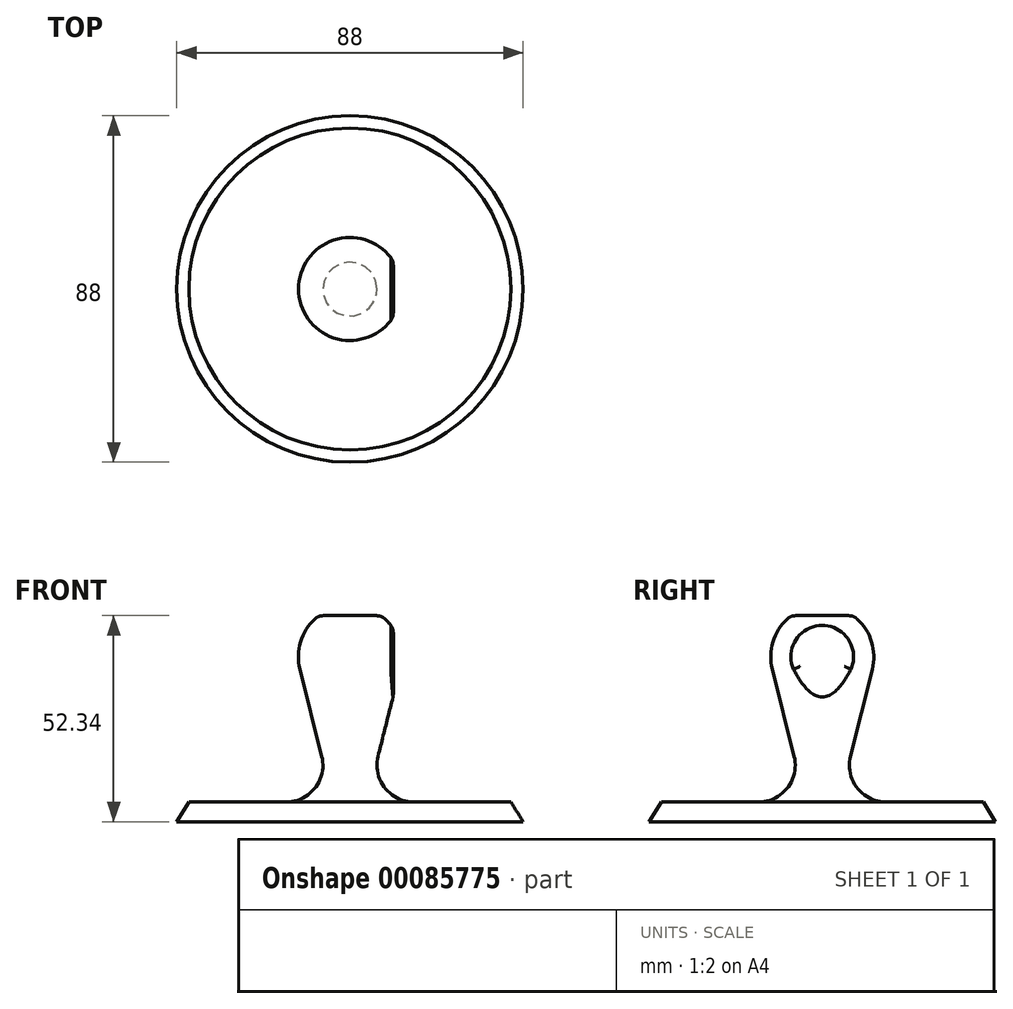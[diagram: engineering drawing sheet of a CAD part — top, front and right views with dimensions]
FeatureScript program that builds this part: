
annotation { "Feature Type Name" : "Feature", "Feature Type Description" : "" }
export const myFeature = defineFeature(function(context is Context, id is Id, definition is map)
    precondition{}
    {
        {
            var Q0;
            Q0=qCreatedBy(makeId("Front.planeOp"),FACE);
            var sketch = newSketch(context, id + "F0", { "sketchPlane" : qUnion([Q0])});
            skLineSegment(sketch, "E0", {"start": v(0, 0) * mm, "end": v(44, 0) * mm});
            skLineSegment(sketch, "E1", {"start": v(44, 0) * mm, "end": v(40.9, 5) * mm});
            skLineSegment(sketch, "E2", {"start": v(40.9, 5) * mm, "end": v(16.23, 5) * mm});
            skArc(sketch, "E3", {"start": v(7.15, 16.63) * mm, "mid": v(8.85, 8.6) * mm, "end": v(16.23, 5) * mm});
            skLineSegment(sketch, "E4", {"start": v(7.15, 16.63) * mm, "end": v(12.7, 38.73) * mm});
            skArc(sketch, "E5", {"start": v(12.7, 38.73) * mm, "mid": v(10.32, 49.96) * mm, "end": v(0, 55) * mm});
            skLineSegment(sketch, "E6", {"start": v(0, 55) * mm, "end": v(0, 0) * mm});
            skLineSegment(sketch, "E7", {"start": v(0, 65.54) * mm, "end": v(0, -37.2) * mm, "construction": true});
            skSolve(sketch);
        }
        {
            var Q0;
            Q0 = qSketchRegion(id + "F0", true);
            var Q1;
            Q1=sQuery(id+"F0.wireOp",EDGE,"E7");
            revolve(context, id + "F1", {"entities" : qUnion([Q0]), "axis" : qUnion([Q1]), "revolveType" : RevolveType.FULL});
        }
        {
            var Q0;
            Q0=qCreatedBy(makeId("Top.planeOp"),FACE);
            cPlane(context, id + "F2", {"entities" : qUnion([Q0]), "cplaneType" : CPlaneType.OFFSET, "offset" : 56 * mm, "width" : 150 * mm, "height" : 150 * mm});
        }
        {
            var Q0;
            Q0=qCreatedBy(id+"F2.planeOp",FACE);
            var sketch = newSketch(context, id + "F3", { "sketchPlane" : qUnion([Q0])});
            skLineSegment(sketch, "E8.bottom", {"start": v(11, 15.97) * mm, "end": v(25, 15.97) * mm});
            skLineSegment(sketch, "E8.top", {"start": v(11, -23.82) * mm, "end": v(25, -23.82) * mm});
            skLineSegment(sketch, "E8.left", {"start": v(11, 15.97) * mm, "end": v(11, -23.82) * mm});
            skLineSegment(sketch, "E8.right", {"start": v(25, 15.97) * mm, "end": v(25, -23.82) * mm});
            skSolve(sketch);
        }
        {
            var Q0;
            Q0=makeQuery(id+"F3.imprint","IMPRINT",FACE,{"disambiguationData":[TD([[makeQuery(id+"F3.imprint","IMPRINT",EDGE,{"derivedFrom":sQuery(id+"F3.wireOp",EDGE,"E8.bottom")}),-1.0]])]});
            extrude(context, id + "F4", {"entities" : qUnion([Q0]), "operationType" : NewBodyOperationType.REMOVE, "oppositeDirection" : true, "depth" : 25 * mm});
        }
        {
            var Q0;
            Q0=qCreatedBy(makeId("Front.planeOp"),FACE);
            var sketch = newSketch(context, id + "F5", { "sketchPlane" : qUnion([Q0])});
            skLineSegment(sketch, "E9.bottom", {"start": v(-16.75, 61.5) * mm, "end": v(29.24, 61.5) * mm});
            skLineSegment(sketch, "E9.top", {"start": v(-16.75, 52.34) * mm, "end": v(29.24, 52.34) * mm});
            skLineSegment(sketch, "E9.left", {"start": v(-16.75, 61.5) * mm, "end": v(-16.75, 52.34) * mm});
            skLineSegment(sketch, "E9.right", {"start": v(29.24, 61.5) * mm, "end": v(29.24, 52.34) * mm});
            skSolve(sketch);
        }
        {
            var Q0;
            Q0=makeQuery(id+"F5.imprint","IMPRINT",FACE,{"disambiguationData":[TD([[makeQuery(id+"F5.imprint","IMPRINT",EDGE,{"derivedFrom":sQuery(id+"F5.wireOp",EDGE,"E9.bottom")}),-1.0]])]});
            extrude(context, id + "F6", {"entities" : qUnion([Q0]), "operationType" : NewBodyOperationType.REMOVE, "endBound" : BoundingType.SYMMETRIC, "oppositeDirection" : true, "depth" : 25 * mm});
        }
        {
            var Q0;
            Q0=makeQuery(id+"F6.boolean.opBoolean","INTERSECT",EDGE,{"derivedFrom":[makeQuery(id+"F1.opRevolve","SWEPT_FACE",FACE,{"disambiguationData":[OSD([sQuery(id+"F0.wireOp",EDGE,"E5")])]}),makeQuery(id+"F6.opExtrude","SWEPT_FACE",FACE,{"disambiguationData":[OSD([sQuery(id+"F5.wireOp",EDGE,"E9.top")])]})]});
            var Q1;
            Q1=makeQuery(id+"F4.boolean.opBoolean","INTERSECT",EDGE,{"derivedFrom":[makeQuery(id+"F1.opRevolve","SWEPT_FACE",FACE,{"disambiguationData":[OSD([sQuery(id+"F0.wireOp",EDGE,"E5")])]}),makeQuery(id+"F4.opExtrude","SWEPT_FACE",FACE,{"disambiguationData":[OSD([sQuery(id+"F3.wireOp",EDGE,"E8.left")])]})]});
            var Q2;
            Q2=makeQuery(id+"F4.boolean.opBoolean","INTERSECT",EDGE,{"derivedFrom":[makeQuery(id+"F1.opRevolve","SWEPT_FACE",FACE,{"disambiguationData":[OSD([sQuery(id+"F0.wireOp",EDGE,"E4")])]}),makeQuery(id+"F4.opExtrude","SWEPT_FACE",FACE,{"disambiguationData":[OSD([sQuery(id+"F3.wireOp",EDGE,"E8.left")])]})]});
            fillet(context, id + "F7", {"entities" : qUnion([Q0, Q1, Q2]), "radius" : 3 * mm, "tangentPropagation" : true, "allowEdgeOverflow" : false});
        }
    });
